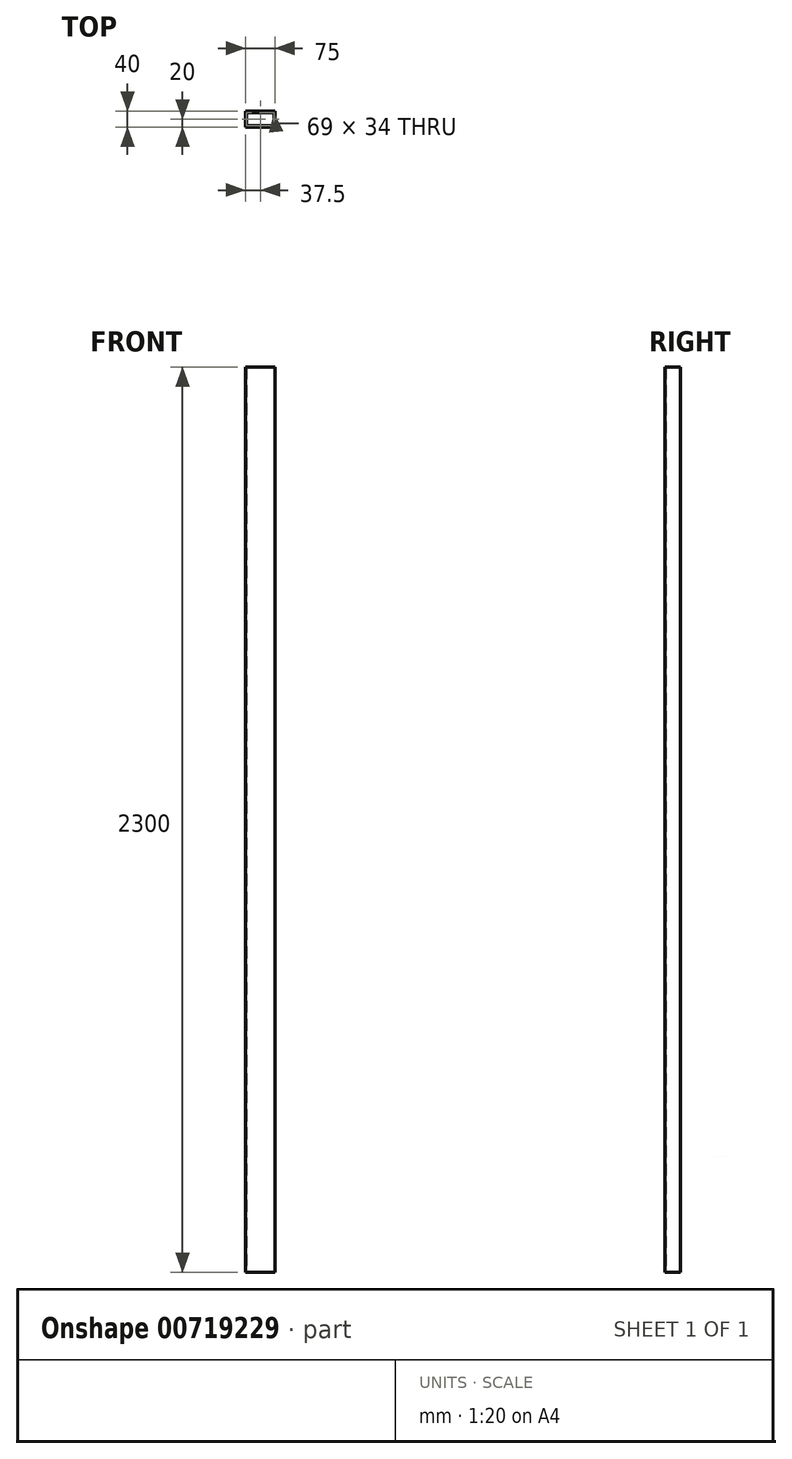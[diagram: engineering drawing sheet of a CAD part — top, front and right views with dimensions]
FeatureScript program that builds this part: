
annotation { "Feature Type Name" : "Feature", "Feature Type Description" : "" }
export const myFeature = defineFeature(function(context is Context, id is Id, definition is map)
    precondition{}
    {
        {
            var Q0;
            Q0=qCreatedBy(makeId("Top.planeOp"),FACE);
            var sketch = newSketch(context, id + "F0", { "sketchPlane" : qUnion([Q0])});
            skLineSegment(sketch, "E0.bottom", {"start": v(0, 0) * mm, "end": v(-75, 0) * mm});
            skLineSegment(sketch, "E0.top", {"start": v(0, 40) * mm, "end": v(-75, 40) * mm});
            skLineSegment(sketch, "E0.left", {"start": v(0, 0) * mm, "end": v(0, 40) * mm});
            skLineSegment(sketch, "E0.right", {"start": v(-75, 0) * mm, "end": v(-75, 40) * mm});
            skLineSegment(sketch, "E1.0", {"start": v(-3, 37) * mm, "end": v(-72, 37) * mm});
            skLineSegment(sketch, "E1.1", {"start": v(-3, 3) * mm, "end": v(-3, 37) * mm});
            skLineSegment(sketch, "E1.2", {"start": v(-3, 3) * mm, "end": v(-72, 3) * mm});
            skLineSegment(sketch, "E1.3", {"start": v(-72, 3) * mm, "end": v(-72, 37) * mm});
            skSolve(sketch);
        }
        {
            var Q0;
            Q0 = qSketchRegion(id + "F0", true);
            extrude(context, id + "F1", {"entities" : qUnion([Q0]), "depth" : 2300 * mm, "offsetDistance" : 25 * mm});
        }
    });
